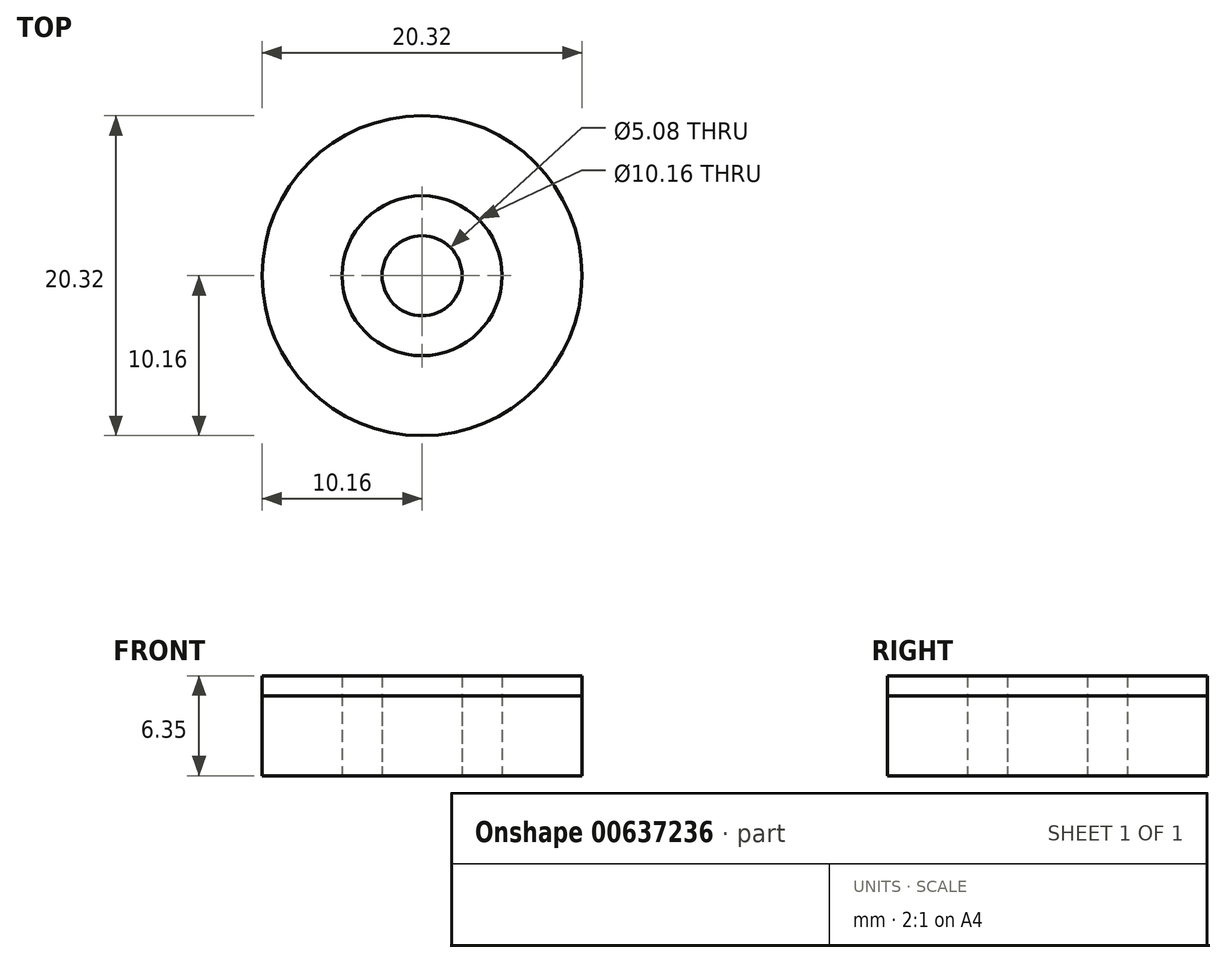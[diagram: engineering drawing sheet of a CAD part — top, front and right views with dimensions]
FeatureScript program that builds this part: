
annotation { "Feature Type Name" : "Feature", "Feature Type Description" : "" }
export const myFeature = defineFeature(function(context is Context, id is Id, definition is map)
    precondition{}
    {
        {
            var Q0;
            Q0=qCreatedBy(makeId("Top.planeOp"),FACE);
            var sketch = newSketch(context, id + "F0", { "sketchPlane" : qUnion([Q0])});
            skCircle(sketch, "E0", {"center": v(0, 0) * mm, "radius": 10.16 * mm});
            skCircle(sketch, "E1", {"center": v(0, 0) * mm, "radius": 5.08 * mm});
            skCircle(sketch, "E2", {"center": v(0, 0) * mm, "radius": 2.54 * mm});
            skSolve(sketch);
        }
        {
            var Q0;
            Q0=makeQuery(id+"F0.imprint","IMPRINT",FACE,{"disambiguationData":[TD([[makeQuery(id+"F0.imprint","IMPRINT",EDGE,{"derivedFrom":sQuery(id+"F0.wireOp",EDGE,"E0")}),1.0]])]});
            var Q1;
            Q1=makeQuery(id+"F0.imprint","IMPRINT",FACE,{"disambiguationData":[TD([[makeQuery(id+"F0.imprint","IMPRINT",EDGE,{"derivedFrom":sQuery(id+"F0.wireOp",EDGE,"E2")}),1.0]])]});
            extrude(context, id + "F1", {"entities" : qUnion([Q0, Q1]), "depth" : 6.35 * mm, "offsetDistance" : 25.4 * mm});
        }
        {
            var Q0;
            Q0 = qSketchRegion(id + "F0", true);
            var Q1;
            Q1=makeQuery(id+"F0.imprint","IMPRINT",FACE,{"disambiguationData":[TD([[makeQuery(id+"F0.imprint","IMPRINT",EDGE,{"derivedFrom":sQuery(id+"F0.wireOp",EDGE,"E1")}),1.0]])]});
            extrude(context, id + "F2", {"entities" : qUnion([Q0, Q1]), "depth" : 5.08 * mm, "offsetDistance" : 25.4 * mm});
        }
    });
